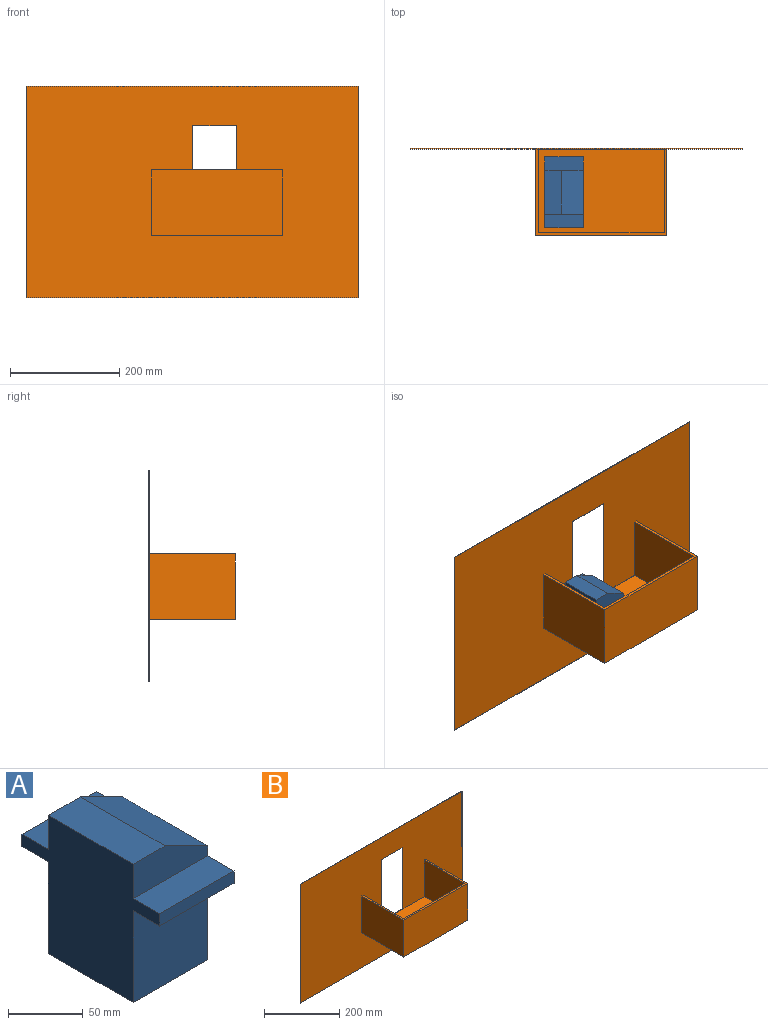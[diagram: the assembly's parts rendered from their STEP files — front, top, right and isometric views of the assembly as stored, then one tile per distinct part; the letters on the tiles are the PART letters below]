
ASSEMBLY  parts=2 mates=1
PART A: 15 faces, bbox 70x130x113 mm
  f0: plane 75x70mm, normal (0,1,0), area 5250mm2, adj f3,f5,f7,f12
  f1: plane 75x70mm, normal (0,-1,0), area 5250mm2, adj f3,f5,f7,f9
  f2: plane 70x28mm, normal (0,1,0), area 1560mm2, adj f3,f5,f6,f11,f14
  f3: plane 130x113mm, normal (-1,0,0), area 9540mm2, adj f0,f1,f2,f4,f6,f7,f8,f9
  f4: plane 70x28mm, normal (0,-1,0), area 1560mm2, adj f3,f5,f6,f10,f14
  f5: plane 130x93mm, normal (1,0,0), area 7940mm2, adj f0,f1,f2,f4,f7,f8,f9,f10
  f6: plane 80x30mm, normal (0,0,1), area 2400mm2, adj f2,f3,f4,f14
  f7: plane 80x70mm, normal (0,0,-1), area 5600mm2, adj f0,f1,f3,f5
  f8: plane 70x10mm, normal (0,-1,0), area 700mm2, adj f3,f5,f9,f10
  f9: plane 70x25mm, normal (0,0,-1), area 1750mm2, adj f1,f3,f5,f8
  f10: plane 70x25mm, normal (0,0,1), area 1750mm2, adj f3,f4,f5,f8
  f11: plane 70x25mm, normal (0,0,1), area 1750mm2, adj f2,f3,f5,f13
  f12: plane 70x25mm, normal (0,0,-1), area 1750mm2, adj f0,f3,f5,f13
  f13: plane 70x10mm, normal (0,1,0), area 700mm2, adj f3,f5,f11,f12
  f14: plane 80x40mm, normal (0.45,0,0.89), area 3577.7mm2, adj f2,f4,f5,f6
PART B: 18 faces, bbox 607.1x159x386.9 mm
  f0: plane 230x154mm, normal (0,0,1), area 35270mm2, adj f2,f3,f4,f12,f14,f16,f17
  f1: plane 240x158mm, normal (0,0,-1), area 37920mm2, adj f5,f6,f7,f17
  f2: plane 153x119mm, normal (-1,0,0), area 18207mm2, adj f0,f4,f8,f17
  f3: plane 153x119mm, normal (1,0,0), area 18207mm2, adj f0,f4,f8,f17
  f4: plane 230x119mm, normal (0,1,0), area 27370mm2, adj f0,f2,f3,f8
  f5: plane 158x120mm, normal (1,0,0), area 18960mm2, adj f1,f6,f8,f17
  f6: plane 240x120mm, normal (0,-1,0), area 28800mm2, adj f1,f5,f7,f8
  f7: plane 158x120mm, normal (-1,0,0), area 18960mm2, adj f1,f6,f8,f17
  f8: plane 240x158mm, normal (0,0,1), area 2730mm2, adj f2,f3,f4,f5,f6,f7,f17
  f9: plane 386.9x1mm, normal (1,0,0), area 386.9mm2, adj f10,f15,f16,f17
  f10: plane 607.13x1mm, normal (0,0,-1), area 607.1mm2, adj f9,f11,f16,f17
  f11: plane 386.9x1mm, normal (-1,0,0), area 386.9mm2, adj f10,f15,f16,f17
  f12: plane 200x1mm, normal (-1,0,0), area 200mm2, adj f0,f13,f16,f17
  f13: plane 80x1mm, normal (0,0,-1), area 80mm2, adj f12,f14,f16,f17
  f14: plane 200x1mm, normal (1,0,0), area 200mm2, adj f0,f13,f16,f17
  f15: plane 607.13x1mm, normal (0,0,1), area 607.1mm2, adj f9,f11,f16,f17
  f16: plane 607.13x386.9mm, normal (0,1,0), area 218899.2mm2, adj f0,f9,f10,f11,f12,f13,f14,f15
  f17: plane 607.13x386.9mm, normal (0,-1,0), area 217469.2mm2, adj f0,f1,f2,f3,f5,f7,f8,f9
PLACE A t=(-39.01,-137.19,70.29)mm
PLACE B t=(-40.83,-128.19,70.29)mm fixed
MATE planar B.f0 <-> A.f7  axis (0,0,1) through (-155.84,-51.51,71.29)mm
